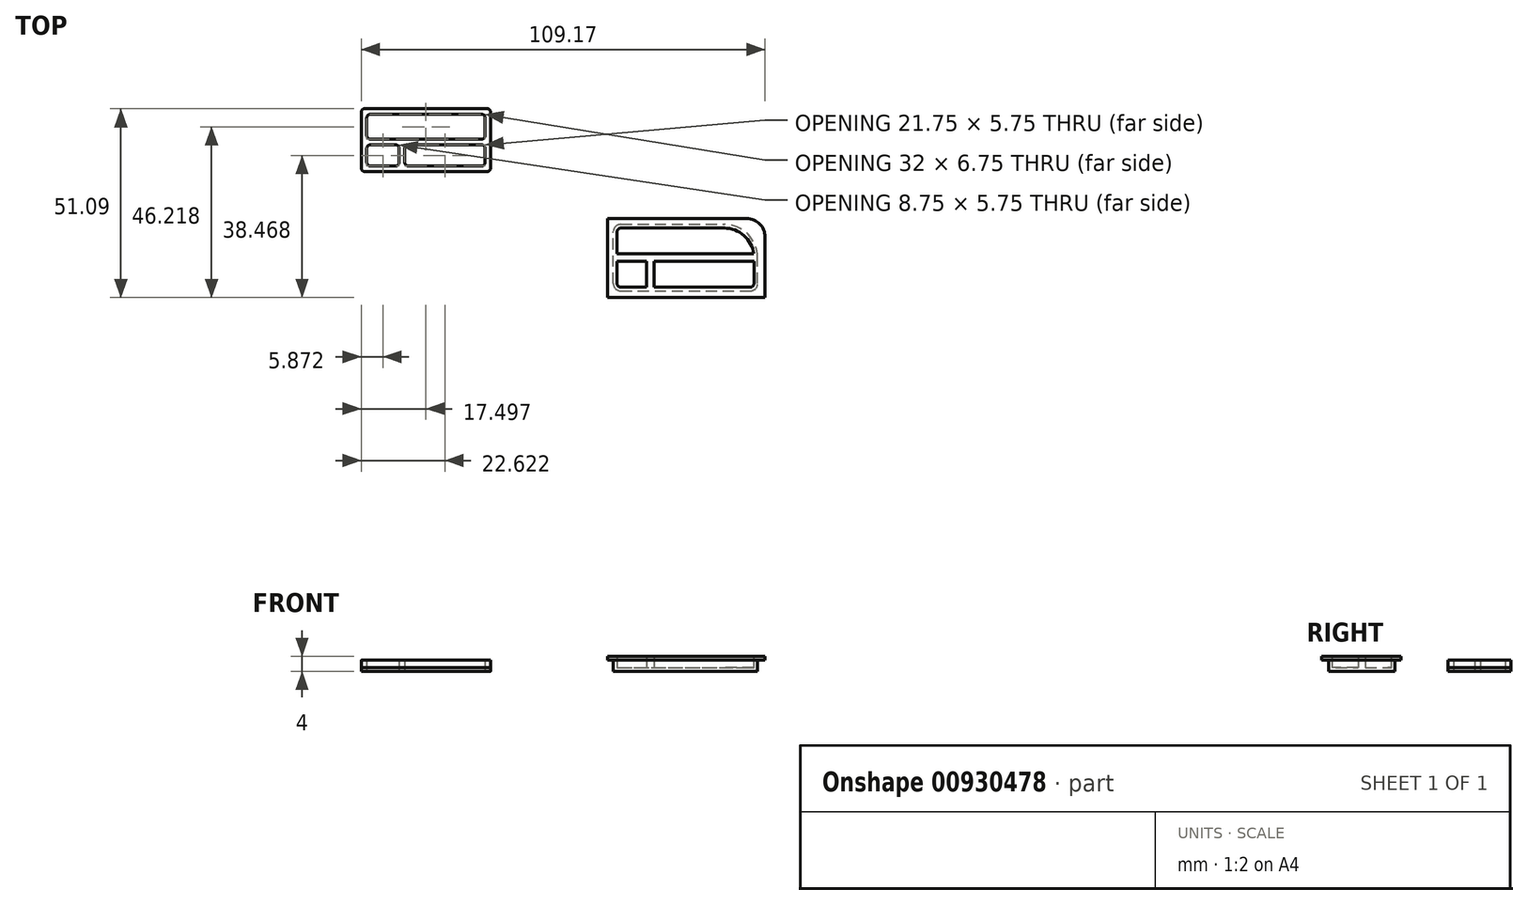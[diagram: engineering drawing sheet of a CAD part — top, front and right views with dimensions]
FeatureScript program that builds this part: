
annotation { "Feature Type Name" : "Feature", "Feature Type Description" : "" }
export const myFeature = defineFeature(function(context is Context, id is Id, definition is map)
    precondition{}
    {
        {
            var Q0;
            Q0=qCreatedBy(makeId("Top.planeOp"),FACE);
            var sketch = newSketch(context, id + "F0", { "sketchPlane" : qUnion([Q0])});
            skLineSegment(sketch, "E0.bottom", {"start": v(1, 0) * mm, "end": v(34, 0) * mm});
            skLineSegment(sketch, "E0.top", {"start": v(1, 17) * mm, "end": v(34, 17) * mm});
            skLineSegment(sketch, "E0.left", {"start": v(0, 1) * mm, "end": v(0, 16) * mm});
            skLineSegment(sketch, "E0.right", {"start": v(35, 1) * mm, "end": v(35, 16) * mm});
            skLineSegment(sketch, "E1", {"start": v(0, 8) * mm, "end": v(35, 8) * mm});
            skLineSegment(sketch, "E2", {"start": v(11, 8) * mm, "end": v(11, 0) * mm});
            skPoint(sketch, "E3.visualSharp", {"position": v(0, 17) * mm});
            skArc(sketch, "E3.filletArc", {"start": v(1, 17) * mm, "mid": v(0.3, 16.7) * mm, "end": v(0, 16) * mm});
            skPoint(sketch, "E4.visualSharp", {"position": v(35, 17) * mm});
            skArc(sketch, "E4.filletArc", {"start": v(35, 16) * mm, "mid": v(34.7, 16.7) * mm, "end": v(34, 17) * mm});
            skPoint(sketch, "E5.visualSharp", {"position": v(35, 0) * mm});
            skArc(sketch, "E5.filletArc", {"start": v(34, 0) * mm, "mid": v(34.7, 0.3) * mm, "end": v(35, 1) * mm});
            skPoint(sketch, "E6.visualSharp", {"position": v(0, 0) * mm});
            skArc(sketch, "E6.filletArc", {"start": v(0, 1) * mm, "mid": v(0.3, 0.3) * mm, "end": v(1, 0) * mm});
            skLineSegment(sketch, "E7.bottom", {"start": v(-39.33, 2.03) * mm, "end": v(-6.33, 2.03) * mm});
            skLineSegment(sketch, "E7.top", {"start": v(-39.33, 19.03) * mm, "end": v(-6.33, 19.03) * mm});
            skLineSegment(sketch, "E7.left", {"start": v(-40.33, 3.03) * mm, "end": v(-40.33, 18.03) * mm});
            skLineSegment(sketch, "E7.right", {"start": v(-5.33, 3.03) * mm, "end": v(-5.33, 18.03) * mm});
            skPoint(sketch, "E8.visualSharp", {"position": v(-40.33, 19.03) * mm});
            skPoint(sketch, "E9.visualSharp", {"position": v(-5.33, 19.03) * mm});
            skPoint(sketch, "E10.visualSharp", {"position": v(-5.33, 2.03) * mm});
            skPoint(sketch, "E11.visualSharp", {"position": v(-40.33, 2.03) * mm});
            skLineSegment(sketch, "E12.0", {"start": v(-37.83, 17.53) * mm, "end": v(-7.83, 17.53) * mm});
            skLineSegment(sketch, "E13.0", {"start": v(-38.83, 4.53) * mm, "end": v(-38.83, 8.28) * mm});
            skLineSegment(sketch, "E14.0", {"start": v(-6.83, 4.53) * mm, "end": v(-6.83, 8.28) * mm});
            skLineSegment(sketch, "E15.0", {"start": v(-27.58, 9.28) * mm, "end": v(-7.83, 9.28) * mm});
            skLineSegment(sketch, "E16.0", {"start": v(-37.83, 10.78) * mm, "end": v(-7.83, 10.78) * mm});
            skLineSegment(sketch, "E17.0", {"start": v(-27.58, 3.53) * mm, "end": v(-7.83, 3.53) * mm});
            skLineSegment(sketch, "E18.0", {"start": v(-30.08, 8.28) * mm, "end": v(-30.08, 4.53) * mm});
            skLineSegment(sketch, "E19.0", {"start": v(-28.58, 8.28) * mm, "end": v(-28.58, 4.53) * mm});
            skArc(sketch, "E20.filletArc", {"start": v(-39.33, 19.03) * mm, "mid": v(-40.04, 18.74) * mm, "end": v(-40.33, 18.03) * mm});
            skArc(sketch, "E21.filletArc", {"start": v(-37.83, 17.53) * mm, "mid": v(-38.54, 17.24) * mm, "end": v(-38.83, 16.53) * mm});
            skArc(sketch, "E22.filletArc", {"start": v(-5.33, 18.03) * mm, "mid": v(-5.63, 18.74) * mm, "end": v(-6.33, 19.03) * mm});
            skArc(sketch, "E23.filletArc", {"start": v(-6.83, 16.53) * mm, "mid": v(-7.13, 17.24) * mm, "end": v(-7.83, 17.53) * mm});
            skArc(sketch, "E24.filletArc", {"start": v(-7.83, 3.53) * mm, "mid": v(-7.13, 3.83) * mm, "end": v(-6.83, 4.53) * mm});
            skArc(sketch, "E25.filletArc", {"start": v(-6.83, 8.28) * mm, "mid": v(-7.13, 8.99) * mm, "end": v(-7.83, 9.28) * mm});
            skArc(sketch, "E26.filletArc", {"start": v(-27.58, 9.28) * mm, "mid": v(-28.3, 8.99) * mm, "end": v(-28.58, 8.28) * mm});
            skArc(sketch, "E27.filletArc", {"start": v(-28.58, 4.53) * mm, "mid": v(-28.3, 3.83) * mm, "end": v(-27.58, 3.53) * mm});
            skLineSegment(sketch, "E28", {"start": v(-38.83, 16.53) * mm, "end": v(-38.83, 11.78) * mm});
            skLineSegment(sketch, "E29", {"start": v(-6.83, 16.53) * mm, "end": v(-6.83, 11.78) * mm});
            skLineSegment(sketch, "E30", {"start": v(-31.08, 3.53) * mm, "end": v(-37.83, 3.53) * mm});
            skArc(sketch, "E31.filletArc", {"start": v(-38.83, 4.53) * mm, "mid": v(-38.54, 3.83) * mm, "end": v(-37.83, 3.53) * mm});
            skArc(sketch, "E32.filletArc", {"start": v(-31.08, 3.53) * mm, "mid": v(-30.38, 3.83) * mm, "end": v(-30.08, 4.53) * mm});
            skArc(sketch, "E33.filletArc", {"start": v(-38.83, 11.78) * mm, "mid": v(-38.54, 11.08) * mm, "end": v(-37.83, 10.78) * mm});
            skArc(sketch, "E34.filletArc", {"start": v(-7.83, 10.78) * mm, "mid": v(-7.13, 11.08) * mm, "end": v(-6.83, 11.78) * mm});
            skArc(sketch, "E35.filletArc", {"start": v(-40.33, 3.03) * mm, "mid": v(-40.04, 2.33) * mm, "end": v(-39.33, 2.03) * mm});
            skLineSegment(sketch, "E36", {"start": v(-31.08, 9.28) * mm, "end": v(-37.83, 9.28) * mm});
            skArc(sketch, "E37.filletArc", {"start": v(-37.83, 9.28) * mm, "mid": v(-38.54, 8.99) * mm, "end": v(-38.83, 8.28) * mm});
            skArc(sketch, "E38.filletArc", {"start": v(-30.08, 8.28) * mm, "mid": v(-30.38, 8.99) * mm, "end": v(-31.08, 9.28) * mm});
            skArc(sketch, "E39.filletArc", {"start": v(-6.33, 2.03) * mm, "mid": v(-5.63, 2.33) * mm, "end": v(-5.33, 3.03) * mm});
            skLineSegment(sketch, "E40.bottom", {"start": v(25.64, 25.67) * mm, "end": v(63.64, 25.67) * mm});
            skLineSegment(sketch, "E40.top", {"start": v(25.64, 43.67) * mm, "end": v(56.64, 43.67) * mm});
            skLineSegment(sketch, "E40.left", {"start": v(23.64, 27.67) * mm, "end": v(23.64, 41.67) * mm});
            skLineSegment(sketch, "E40.right", {"start": v(65.64, 27.67) * mm, "end": v(65.64, 34.67) * mm});
            skPoint(sketch, "E41.visualSharp", {"position": v(65.64, 43.67) * mm});
            skArc(sketch, "E41.filletArc", {"start": v(65.64, 34.67) * mm, "mid": v(63, 41.04) * mm, "end": v(56.64, 43.67) * mm});
            skPoint(sketch, "E42.visualSharp", {"position": v(23.64, 25.67) * mm});
            skArc(sketch, "E42.filletArc", {"start": v(23.64, 27.67) * mm, "mid": v(24.22, 26.26) * mm, "end": v(25.64, 25.67) * mm});
            skPoint(sketch, "E43.visualSharp", {"position": v(23.64, 43.67) * mm});
            skArc(sketch, "E43.filletArc", {"start": v(25.64, 43.67) * mm, "mid": v(24.22, 43.09) * mm, "end": v(23.64, 41.67) * mm});
            skPoint(sketch, "E44.visualSharp", {"position": v(65.64, 25.67) * mm});
            skArc(sketch, "E44.filletArc", {"start": v(63.64, 25.67) * mm, "mid": v(65.05, 26.26) * mm, "end": v(65.64, 27.67) * mm});
            skLineSegment(sketch, "E45.bottom", {"start": v(-42.47, 32.68) * mm, "end": v(-7.47, 32.68) * mm});
            skLineSegment(sketch, "E45.top", {"start": v(-42.47, 50.68) * mm, "end": v(-14.47, 50.68) * mm});
            skLineSegment(sketch, "E45.left", {"start": v(-44.47, 34.68) * mm, "end": v(-44.47, 48.68) * mm});
            skLineSegment(sketch, "E45.right", {"start": v(-5.47, 34.68) * mm, "end": v(-5.47, 41.68) * mm});
            skPoint(sketch, "E46.visualSharp", {"position": v(-5.47, 50.68) * mm});
            skArc(sketch, "E46.filletArc", {"start": v(-5.47, 41.68) * mm, "mid": v(-8.1, 48.05) * mm, "end": v(-14.47, 50.68) * mm});
            skPoint(sketch, "E47.visualSharp", {"position": v(-44.47, 32.68) * mm});
            skArc(sketch, "E47.filletArc", {"start": v(-44.47, 34.68) * mm, "mid": v(-43.89, 33.27) * mm, "end": v(-42.47, 32.68) * mm});
            skPoint(sketch, "E48.visualSharp", {"position": v(-44.47, 50.68) * mm});
            skArc(sketch, "E48.filletArc", {"start": v(-42.47, 50.68) * mm, "mid": v(-43.89, 50.1) * mm, "end": v(-44.47, 48.68) * mm});
            skPoint(sketch, "E49.visualSharp", {"position": v(-5.47, 32.68) * mm});
            skArc(sketch, "E49.filletArc", {"start": v(-7.47, 32.68) * mm, "mid": v(-6.06, 33.27) * mm, "end": v(-5.47, 34.68) * mm});
            skLineSegment(sketch, "E50", {"start": v(-42.86, -34.92) * mm, "end": v(-82.86, -34.92) * mm});
            skLineSegment(sketch, "E51", {"start": v(-72.1, -41.65) * mm, "end": v(-72.1, -49.5) * mm});
            skLineSegment(sketch, "E52", {"start": v(-71.65, -51.86) * mm, "end": v(-71.65, -59.7) * mm});
            skLineSegment(sketch, "E53", {"start": v(-68.08, -49.58) * mm, "end": v(-68.08, -51.96) * mm});
            skLineSegment(sketch, "E54", {"start": v(-78.57, -55.79) * mm, "end": v(-69.5, -55.79) * mm});
            skPoint(sketch, "E54.startSnap0", {"position": v(-71.65, -55.79) * mm});
            skLineSegment(sketch, "E55", {"start": v(-44.47, 41.68) * mm, "end": v(-5.47, 41.68) * mm});
            skLineSegment(sketch, "E56", {"start": v(-44.47, 41.68) * mm, "end": v(-34.47, 41.68) * mm});
            skLineSegment(sketch, "E57", {"start": v(-34.47, 41.68) * mm, "end": v(-34.47, 32.68) * mm});
            skSolve(sketch);
        }
        {
            var Q0;
            Q0=makeQuery(id+"F0.imprint","IMPRINT",FACE,{"disambiguationData":[TD([[makeQuery(id+"F0.imprint","IMPRINT",EDGE,{"derivedFrom":sQuery(id+"F0.wireOp",EDGE,"E7.bottom")}),1.0]])]});
            extrude(context, id + "F1", {"entities" : qUnion([Q0]), "depth" : 3 * mm, "offsetDistance" : 25 * mm});
        }
        {
            var Q0;
            Q0=makeQuery(id+"F0.imprint","IMPRINT",FACE,{"disambiguationData":[TD([[makeQuery(id+"F0.imprint","IMPRINT",EDGE,{"derivedFrom":sQuery(id+"F0.wireOp",EDGE,"E7.bottom")}),1.0]])]});
            var Q1;
            Q1=makeQuery(id+"F0.imprint","IMPRINT",FACE,{"disambiguationData":[TD([[makeQuery(id+"F0.imprint","IMPRINT",EDGE,{"derivedFrom":sQuery(id+"F0.wireOp",EDGE,"E12.0")}),-1.0]])]});
            var Q2;
            Q2=makeQuery(id+"F0.imprint","IMPRINT",FACE,{"disambiguationData":[TD([[makeQuery(id+"F0.imprint","IMPRINT",EDGE,{"derivedFrom":sQuery(id+"F0.wireOp",EDGE,"E14.0")}),1.0]])]});
            var Q3;
            Q3=makeQuery(id+"F0.imprint","IMPRINT",FACE,{"disambiguationData":[TD([[makeQuery(id+"F0.imprint","IMPRINT",EDGE,{"derivedFrom":sQuery(id+"F0.wireOp",EDGE,"E13.0")}),-1.0]])]});
            extrude(context, id + "F2", {"entities" : qUnion([Q0, Q1, Q2, Q3]), "depth" : 1 * mm, "offsetDistance" : 25 * mm});
        }
        {
            var Q0;
            Q0=qCreatedBy(makeId("Top.planeOp"),FACE);
            var sketch = newSketch(context, id + "F3", { "sketchPlane" : qUnion([Q0])});
            skLineSegment(sketch, "E58.bottom", {"start": v(29.83, -30.25) * mm, "end": v(64.83, -30.25) * mm});
            skLineSegment(sketch, "E58.top", {"start": v(29.83, -12.25) * mm, "end": v(57.83, -12.25) * mm});
            skLineSegment(sketch, "E58.left", {"start": v(27.83, -28.25) * mm, "end": v(27.83, -14.25) * mm});
            skLineSegment(sketch, "E58.right", {"start": v(66.83, -28.25) * mm, "end": v(66.83, -21.25) * mm});
            skPoint(sketch, "E59.visualSharp", {"position": v(66.83, -12.25) * mm});
            skArc(sketch, "E59.filletArc", {"start": v(66.83, -21.25) * mm, "mid": v(64.2, -14.89) * mm, "end": v(57.83, -12.25) * mm});
            skPoint(sketch, "E60.visualSharp", {"position": v(27.83, -30.25) * mm});
            skArc(sketch, "E60.filletArc", {"start": v(27.83, -28.25) * mm, "mid": v(28.41, -29.67) * mm, "end": v(29.83, -30.25) * mm});
            skPoint(sketch, "E61.visualSharp", {"position": v(27.83, -12.25) * mm});
            skArc(sketch, "E61.filletArc", {"start": v(29.83, -12.25) * mm, "mid": v(28.41, -12.84) * mm, "end": v(27.83, -14.25) * mm});
            skPoint(sketch, "E62.visualSharp", {"position": v(66.83, -30.25) * mm});
            skArc(sketch, "E62.filletArc", {"start": v(64.83, -30.25) * mm, "mid": v(66.24, -29.67) * mm, "end": v(66.83, -28.25) * mm});
            skLineSegment(sketch, "E63", {"start": v(27.83, -21.25) * mm, "end": v(66.83, -21.25) * mm});
            skLineSegment(sketch, "E64", {"start": v(27.83, -21.25) * mm, "end": v(37.83, -21.25) * mm});
            skLineSegment(sketch, "E65", {"start": v(37.83, -21.25) * mm, "end": v(37.83, -30.25) * mm});
            skSolve(sketch);
        }
        {
            var Q0;
            {var subQ1=sQuery(id+"F3.wireOp",EDGE,"E60.filletArc");Q0=makeQuery(id+"F3.imprint","IMPRINT",FACE,{"disambiguationData":[TD([[makeQuery(id+"F3.imprint","IMPRINT",EDGE,{"derivedFrom":subQ1}),1.0]])]});}
            extrude(context, id + "F4", {"entities" : qUnion([Q0]), "depth" : 4 * mm, "offsetDistance" : 25 * mm});
        }
        {
            var Q0;
            Q0=makeQuery(id+"F4.opExtrude","CAP_FACE",FACE,{"disambiguationData":[OSD([sQuery(id+"F3.wireOp",EDGE,"E58.bottom"),sQuery(id+"F3.wireOp",EDGE,"E58.left"),sQuery(id+"F3.wireOp",EDGE,"E60.filletArc"),sQuery(id+"F3.wireOp",EDGE,"E64"),sQuery(id+"F3.wireOp",EDGE,"E65")])],"isStart":false});
            shell(context, id + "F5", {"entities" : qUnion([Q0]), "thickness" : 1 * mm});
        }
        {
            var Q0;
            Q0=makeQuery(id+"F3.imprint","IMPRINT",FACE,{"disambiguationData":[TD([[makeQuery(id+"F3.imprint","IMPRINT",EDGE,{"derivedFrom":sQuery(id+"F3.wireOp",EDGE,"E58.right")}),1.0]])]});
            extrude(context, id + "F6", {"entities" : qUnion([Q0]), "depth" : 4 * mm, "offsetDistance" : 25 * mm});
        }
        {
            var Q0;
            Q0=makeQuery(id+"F6.opExtrude","CAP_FACE",FACE,{"disambiguationData":[OSD([sQuery(id+"F3.wireOp",EDGE,"E58.bottom"),sQuery(id+"F3.wireOp",EDGE,"E58.right"),sQuery(id+"F3.wireOp",EDGE,"E62.filletArc"),sQuery(id+"F3.wireOp",EDGE,"E63"),sQuery(id+"F3.wireOp",EDGE,"E65")])],"isStart":false});
            shell(context, id + "F7", {"entities" : qUnion([Q0]), "thickness" : 1 * mm});
        }
        {
            var Q0;
            Q0=makeQuery(id+"F3.imprint","IMPRINT",FACE,{"disambiguationData":[TD([[makeQuery(id+"F3.imprint","IMPRINT",EDGE,{"derivedFrom":sQuery(id+"F3.wireOp",EDGE,"E58.top")}),-1.0]])]});
            extrude(context, id + "F8", {"entities" : qUnion([Q0]), "depth" : 4 * mm, "offsetDistance" : 25 * mm});
        }
        {
            var Q0;
            Q0=makeQuery(id+"F8.opExtrude","CAP_FACE",FACE,{"disambiguationData":[OSD([sQuery(id+"F3.wireOp",EDGE,"E58.top"),sQuery(id+"F3.wireOp",EDGE,"E58.left"),sQuery(id+"F3.wireOp",EDGE,"E59.filletArc"),sQuery(id+"F3.wireOp",EDGE,"E61.filletArc"),sQuery(id+"F3.wireOp",EDGE,"E63"),sQuery(id+"F3.wireOp",EDGE,"E64")])],"isStart":false});
            shell(context, id + "F9", {"entities" : qUnion([Q0]), "thickness" : 1 * mm});
        }
        {
            var Q0;
            Q0=makeQuery(id+"F4.opExtrude","SWEPT_BODY",BODY,{"disambiguationData":[OSD([sQuery(id+"F3.wireOp",EDGE,"E58.bottom"),sQuery(id+"F3.wireOp",EDGE,"E58.left"),sQuery(id+"F3.wireOp",EDGE,"E60.filletArc"),sQuery(id+"F3.wireOp",EDGE,"E64"),sQuery(id+"F3.wireOp",EDGE,"E65")])]});
            var Q1;
            Q1=makeQuery(id+"F6.opExtrude","SWEPT_BODY",BODY,{"disambiguationData":[OSD([sQuery(id+"F3.wireOp",EDGE,"E58.bottom"),sQuery(id+"F3.wireOp",EDGE,"E58.right"),sQuery(id+"F3.wireOp",EDGE,"E62.filletArc"),sQuery(id+"F3.wireOp",EDGE,"E63"),sQuery(id+"F3.wireOp",EDGE,"E65")])]});
            var Q2;
            Q2=makeQuery(id+"F8.opExtrude","SWEPT_BODY",BODY,{"disambiguationData":[OSD([sQuery(id+"F3.wireOp",EDGE,"E58.top"),sQuery(id+"F3.wireOp",EDGE,"E58.left"),sQuery(id+"F3.wireOp",EDGE,"E59.filletArc"),sQuery(id+"F3.wireOp",EDGE,"E61.filletArc"),sQuery(id+"F3.wireOp",EDGE,"E63"),sQuery(id+"F3.wireOp",EDGE,"E64")])]});
            booleanBodies(context, id + "F10", {"operationType" : BooleanOperationType.UNION, "tools" : qUnion([Q0, Q1, Q2])});
        }
        {
            var Q0;
            {var subQ0=sQuery(id+"F3.wireOp",EDGE,"E64");var subQ1=sQuery(id+"F3.wireOp",EDGE,"E63");var subQ2=sQuery(id+"F3.wireOp",EDGE,"E58.left");var subQ3=sQuery(id+"F3.wireOp",EDGE,"E65");var subQ4=sQuery(id+"F3.wireOp",EDGE,"E58.bottom");Q0=makeQuery(id+"F10.opBoolean","MERGE",FACE,{"derivedFrom":[makeQuery(id+"F4.opExtrude","CAP_FACE",FACE,{"disambiguationData":[OSD([subQ4,subQ2,sQuery(id+"F3.wireOp",EDGE,"E60.filletArc"),subQ0,subQ3])],"isStart":false}),makeQuery(id+"F6.opExtrude","CAP_FACE",FACE,{"disambiguationData":[OSD([subQ4,sQuery(id+"F3.wireOp",EDGE,"E58.right"),sQuery(id+"F3.wireOp",EDGE,"E62.filletArc"),subQ1,subQ3])],"isStart":false}),makeQuery(id+"F8.opExtrude","CAP_FACE",FACE,{"disambiguationData":[OSD([sQuery(id+"F3.wireOp",EDGE,"E58.top"),subQ2,sQuery(id+"F3.wireOp",EDGE,"E59.filletArc"),sQuery(id+"F3.wireOp",EDGE,"E61.filletArc"),subQ1,subQ0])],"isStart":false})]});}
            var sketch = newSketch(context, id + "F11", { "sketchPlane" : qUnion([Q0])});
            skLineSegment(sketch, "E66.bottom", {"start": v(26.2, -32.06) * mm, "end": v(68.84, -32.06) * mm});
            skLineSegment(sketch, "E66.top", {"start": v(26.2, -10.68) * mm, "end": v(63.84, -10.68) * mm});
            skLineSegment(sketch, "E66.left", {"start": v(26.2, -32.06) * mm, "end": v(26.2, -10.68) * mm});
            skLineSegment(sketch, "E66.right", {"start": v(68.84, -32.06) * mm, "end": v(68.84, -15.68) * mm});
            skPoint(sketch, "E67.visualSharp", {"position": v(68.84, -10.68) * mm});
            skArc(sketch, "E67.filletArc", {"start": v(68.84, -15.68) * mm, "mid": v(67.38, -12.15) * mm, "end": v(63.84, -10.68) * mm});
            skSolve(sketch);
        }
        {
            var Q0;
            {var subQ16=sQuery(id+"F3.wireOp",EDGE,"E60.filletArc");var subQ17=makeQuery(id+"F4.opExtrude","CAP_EDGE",EDGE,{"disambiguationData":[OSD([subQ16])],"isStart":false});Q0=makeQuery(id+"F11.imprint","IMPRINT",FACE,{"disambiguationData":[TD([[makeQuery(id+"F11.imprint","IMPRINT",EDGE,{"derivedFrom":subQ17}),1.0]])]});}
            var Q1;
            Q1=makeQuery(id+"F11.imprint","IMPRINT",FACE,{"disambiguationData":[TD([[makeQuery(id+"F11.imprint","IMPRINT",EDGE,{"derivedFrom":sQuery(id+"F11.wireOp",EDGE,"E66.bottom")}),1.0]])]});
            extrude(context, id + "F12", {"entities" : qUnion([Q0, Q1]), "operationType" : NewBodyOperationType.ADD, "depth" : -1 * mm, "offsetDistance" : 25 * mm});
        }
    });
